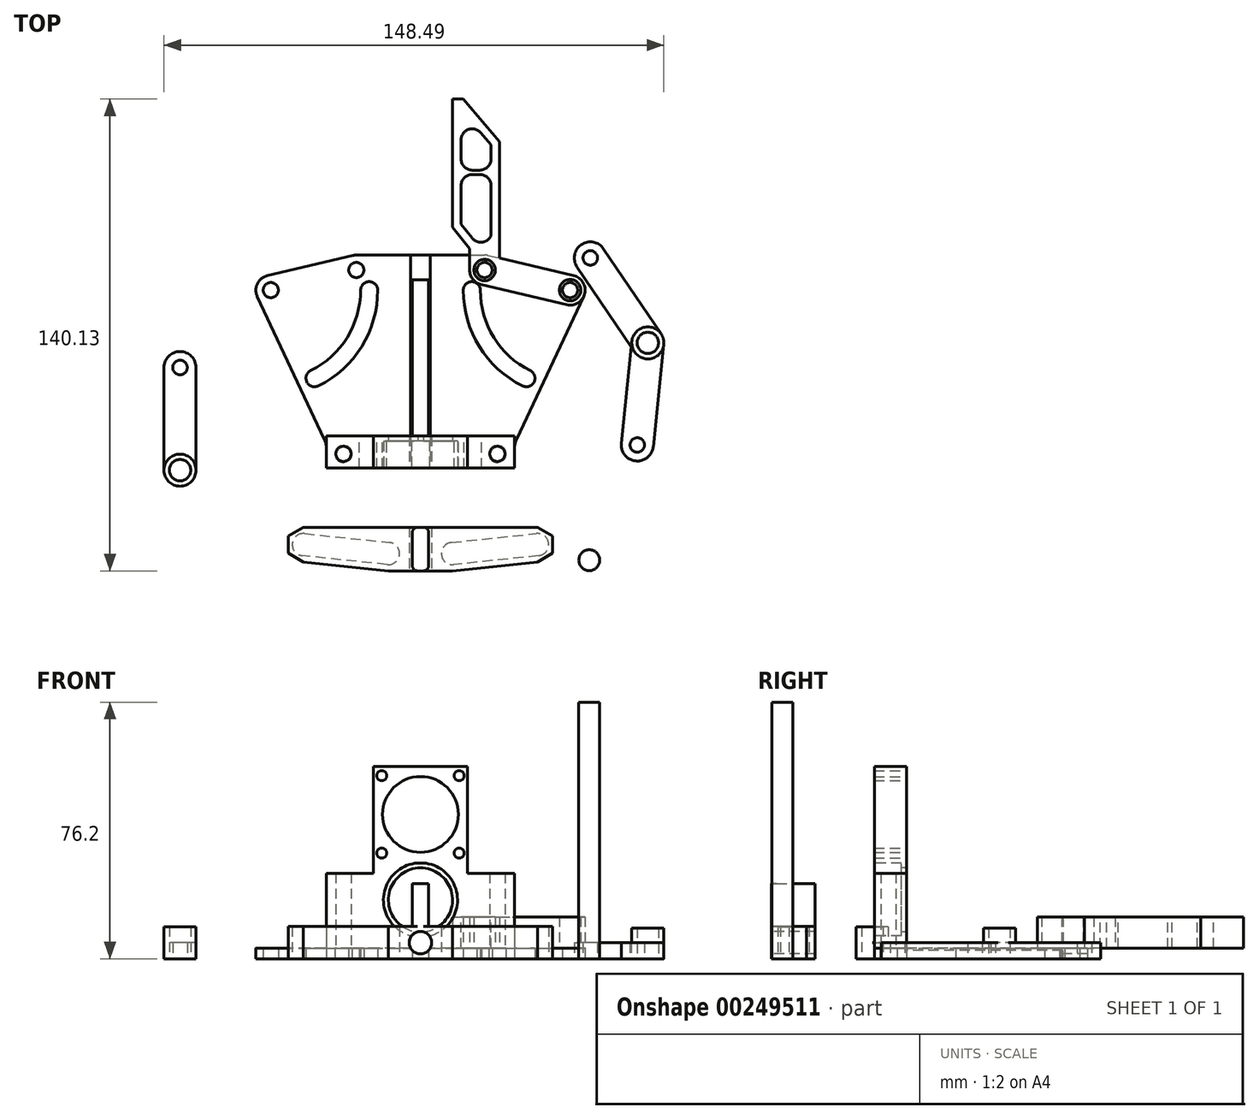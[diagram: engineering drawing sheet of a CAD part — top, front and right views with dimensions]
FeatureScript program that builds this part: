
annotation { "Feature Type Name" : "Feature", "Feature Type Description" : "" }
export const myFeature = defineFeature(function(context is Context, id is Id, definition is map)
    precondition{}
    {
        {
            var Q0;
            Q0=qCreatedBy(makeId("Top.planeOp"),FACE);
            var sketch = newSketch(context, id + "F0", { "sketchPlane" : qUnion([Q0])});
            skLineSegment(sketch, "E0", {"start": v(0, 0) * mm, "end": v(0, 58.8) * mm, "construction": true});
            skLineSegment(sketch, "E1", {"start": v(-19.05, 58.8) * mm, "end": v(19.05, 58.8) * mm, "construction": true});
            skLineSegment(sketch, "E2", {"start": v(-44.45, 52.83) * mm, "end": v(44.45, 52.83) * mm, "construction": true});
            skPoint(sketch, "E3", {"position": v(0, 52.83) * mm});
            skCircle(sketch, "E4", {"center": v(-19.05, 58.8) * mm, "radius": 2.25 * mm});
            skCircle(sketch, "E5", {"center": v(19.05, 58.8) * mm, "radius": 2.25 * mm});
            skCircle(sketch, "E6", {"center": v(44.45, 52.83) * mm, "radius": 2.25 * mm});
            skCircle(sketch, "E7", {"center": v(-44.45, 52.83) * mm, "radius": 2.25 * mm});
            skArc(sketch, "E8", {"start": v(-19.05, 63.25) * mm, "mid": v(-19.56, 63.22) * mm, "end": v(-20.07, 63.13) * mm});
            skArc(sketch, "E9", {"start": v(20.07, 63.13) * mm, "mid": v(19.56, 63.22) * mm, "end": v(19.05, 63.25) * mm});
            skArc(sketch, "E10", {"start": v(48.47, 50.94) * mm, "mid": v(48.45, 54.77) * mm, "end": v(45.47, 57.16) * mm});
            skArc(sketch, "E11", {"start": v(-45.47, 57.16) * mm, "mid": v(-48.45, 54.77) * mm, "end": v(-48.47, 50.94) * mm});
            skLineSegment(sketch, "E12", {"start": v(-28.57, 8.52) * mm, "end": v(-48.47, 50.94) * mm});
            skLineSegment(sketch, "E13", {"start": v(28.57, 8.52) * mm, "end": v(48.47, 50.94) * mm});
            skLineSegment(sketch, "E14", {"start": v(-45.47, 57.16) * mm, "end": v(-20.07, 63.13) * mm});
            skLineSegment(sketch, "E15", {"start": v(-19.05, 63.25) * mm, "end": v(19.05, 63.25) * mm});
            skLineSegment(sketch, "E16", {"start": v(20.07, 63.13) * mm, "end": v(45.47, 57.16) * mm});
            skPoint(sketch, "E17.visualSharp", {"position": v(-38.17, 49.74) * mm});
            skPoint(sketch, "E18.visualSharp", {"position": v(-18.53, 54.36) * mm});
            skPoint(sketch, "E19.visualSharp", {"position": v(38.17, 49.74) * mm});
            skCircle(sketch, "E20", {"center": v(-22.86, 4.2) * mm, "radius": 2.55 * mm});
            skCircle(sketch, "E21", {"center": v(22.86, 4.2) * mm, "radius": 2.55 * mm});
            skLineSegment(sketch, "E22.left", {"start": v(-27.94, 5.72) * mm, "end": v(-27.94, 0) * mm});
            skLineSegment(sketch, "E22.right", {"start": v(27.94, 5.72) * mm, "end": v(27.94, 0) * mm});
            skPoint(sketch, "E23.visualSharp", {"position": v(-27.94, 7.19) * mm});
            skArc(sketch, "E23.filletArc", {"start": v(-27.94, 5.72) * mm, "mid": v(-28.1, 7.15) * mm, "end": v(-28.57, 8.52) * mm});
            skPoint(sketch, "E24.visualSharp", {"position": v(27.94, 7.19) * mm});
            skArc(sketch, "E24.filletArc", {"start": v(28.57, 8.52) * mm, "mid": v(28.1, 7.15) * mm, "end": v(27.94, 5.72) * mm});
            skLineSegment(sketch, "E25", {"start": v(-27.94, 0) * mm, "end": v(-18.16, 0) * mm});
            skLineSegment(sketch, "E26.trimOffspring", {"start": v(18.16, 0) * mm, "end": v(27.94, 0) * mm});
            skLineSegment(sketch, "E27", {"start": v(-18.16, 0) * mm, "end": v(-18.16, 9.52) * mm});
            skLineSegment(sketch, "E28", {"start": v(18.16, 0) * mm, "end": v(18.16, 9.52) * mm});
            skLineSegment(sketch, "E29", {"start": v(-2.44, 55.89) * mm, "end": v(-2.44, 9.52) * mm});
            skLineSegment(sketch, "E30", {"start": v(-2.44, 9.52) * mm, "end": v(-18.16, 9.52) * mm});
            skLineSegment(sketch, "E31", {"start": v(18.16, 9.52) * mm, "end": v(2.44, 9.52) * mm});
            skLineSegment(sketch, "E32", {"start": v(2.44, 9.52) * mm, "end": v(2.44, 55.89) * mm});
            skLineSegment(sketch, "E33", {"start": v(-2.44, 55.89) * mm, "end": v(2.44, 55.89) * mm});
            skArc(sketch, "E34", {"start": v(15.24, 52.83) * mm, "mid": v(19.63, 37.44) * mm, "end": v(31.47, 26.67) * mm, "construction": true});
            skArc(sketch, "E35", {"start": v(17.78, 52.83) * mm, "mid": v(15.24, 55.37) * mm, "end": v(12.7, 52.83) * mm});
            skLineSegment(sketch, "E36", {"start": v(44.45, 52.83) * mm, "end": v(22.86, 4.2) * mm, "construction": true});
            skArc(sketch, "E37", {"start": v(32.6, 28.94) * mm, "mid": v(21.79, 38.78) * mm, "end": v(17.78, 52.83) * mm});
            skArc(sketch, "E38", {"start": v(12.7, 52.83) * mm, "mid": v(17.47, 36.1) * mm, "end": v(30.34, 24.39) * mm});
            skArc(sketch, "E39", {"start": v(30.34, 24.39) * mm, "mid": v(33.74, 25.54) * mm, "end": v(32.6, 28.94) * mm});
            skArc(sketch, "E40.MirrorCS", {"start": v(-30.34, 24.39) * mm, "mid": v(-33.74, 25.54) * mm, "end": v(-32.6, 28.94) * mm});
            skArc(sketch, "E41.MirrorCS", {"start": v(-32.6, 28.94) * mm, "mid": v(-21.79, 38.78) * mm, "end": v(-17.78, 52.83) * mm});
            skArc(sketch, "E42.MirrorCS", {"start": v(-12.7, 52.83) * mm, "mid": v(-17.47, 36.1) * mm, "end": v(-30.34, 24.39) * mm});
            skArc(sketch, "E43.MirrorCS", {"start": v(-17.78, 52.83) * mm, "mid": v(-15.24, 55.37) * mm, "end": v(-12.7, 52.83) * mm});
            skSolve(sketch);
        }
        {
            var Q0;
            Q0 = qSketchRegion(id + "F0", true);
            extrude(context, id + "F1", {"entities" : qUnion([Q0]), "depth" : 3.17 * mm});
        }
        {
            var Q0;
            Q0=qCreatedBy(makeId("Top.planeOp"),FACE);
            var sketch = newSketch(context, id + "F2", { "sketchPlane" : qUnion([Q0])});
            skCircle(sketch, "E44", {"center": v(-71.43, -0.63) * mm, "radius": 3.18 * mm});
            skCircle(sketch, "E45", {"center": v(-71.43, 29.85) * mm, "radius": 2.16 * mm});
            skCircle(sketch, "E46", {"center": v(-71.43, 29.85) * mm, "radius": 4.76 * mm});
            skCircle(sketch, "E47", {"center": v(-71.43, -0.63) * mm, "radius": 4.76 * mm});
            skLineSegment(sketch, "E48", {"start": v(-76.2, -0.63) * mm, "end": v(-76.2, 29.85) * mm});
            skLineSegment(sketch, "E49", {"start": v(-66.67, 29.85) * mm, "end": v(-66.67, -0.63) * mm});
            skSolve(sketch);
        }
        {
            var Q0;
            Q0 = qSketchRegion(id + "F2", true);
            extrude(context, id + "F3", {"entities" : qUnion([Q0]), "depth" : 4.76 * mm});
        }
        {
            var Q0;
            Q0=qCreatedBy(makeId("Top.planeOp"),FACE);
            var sketch = newSketch(context, id + "F4", { "sketchPlane" : qUnion([Q0])});
            skCircle(sketch, "E50", {"center": v(64.4, 6.85) * mm, "radius": 2.16 * mm});
            skCircle(sketch, "E51", {"center": v(67.54, 37.16) * mm, "radius": 3.18 * mm});
            skCircle(sketch, "E52", {"center": v(50.46, 62.4) * mm, "radius": 2.16 * mm});
            skLineSegment(sketch, "E53", {"start": v(50.46, 62.4) * mm, "end": v(67.54, 37.16) * mm, "construction": true});
            skLineSegment(sketch, "E54", {"start": v(67.54, 37.16) * mm, "end": v(64.4, 6.85) * mm, "construction": true});
            skArc(sketch, "E55", {"start": v(54.4, 65.08) * mm, "mid": v(47.79, 66.35) * mm, "end": v(46.51, 59.74) * mm});
            skArc(sketch, "E56", {"start": v(72.28, 36.67) * mm, "mid": v(72.16, 38.32) * mm, "end": v(71.48, 39.83) * mm});
            skLineSegment(sketch, "E57", {"start": v(54.4, 65.08) * mm, "end": v(71.48, 39.83) * mm});
            skLineSegment(sketch, "E58", {"start": v(72.28, 36.67) * mm, "end": v(69.14, 6.36) * mm});
            skLineSegment(sketch, "E59", {"start": v(59.66, 7.34) * mm, "end": v(62.62, 35.93) * mm});
            skLineSegment(sketch, "E60", {"start": v(62.62, 35.93) * mm, "end": v(46.51, 59.74) * mm});
            skCircle(sketch, "E61", {"center": v(64.4, 6.85) * mm, "radius": 4.76 * mm});
            skSolve(sketch);
        }
        {
            var Q0;
            Q0 = qSketchRegion(id + "F4", true);
            extrude(context, id + "F5", {"entities" : qUnion([Q0]), "depth" : 4.76 * mm});
        }
        {
            var Q0;
            Q0=makeQuery(id+"F1.opExtrude","CAP_FACE",FACE,{"disambiguationData":[OSD([sQuery(id+"F0.wireOp",EDGE,"E4"),sQuery(id+"F0.wireOp",EDGE,"E5"),sQuery(id+"F0.wireOp",EDGE,"E6"),sQuery(id+"F0.wireOp",EDGE,"E7"),sQuery(id+"F0.wireOp",EDGE,"E8"),sQuery(id+"F0.wireOp",EDGE,"E9"),sQuery(id+"F0.wireOp",EDGE,"E10"),sQuery(id+"F0.wireOp",EDGE,"E11"),sQuery(id+"F0.wireOp",EDGE,"CqgLeqqC-iIWA-dWGX-UMBu-9zdK8dDdMv7x"),sQuery(id+"F0.wireOp",EDGE,"E12"),sQuery(id+"F0.wireOp",EDGE,"E13"),sQuery(id+"F0.wireOp",EDGE,"E14"),sQuery(id+"F0.wireOp",EDGE,"E15"),sQuery(id+"F0.wireOp",EDGE,"E16"),sQuery(id+"F0.wireOp",EDGE,"d945b0c3-6755-44a5-947e-2b61b1ff6794.0"),sQuery(id+"F0.wireOp",EDGE,"d945b0c3-6755-44a5-947e-2b61b1ff6794.1"),sQuery(id+"F0.wireOp",EDGE,"d945b0c3-6755-44a5-947e-2b61b1ff6794.2"),sQuery(id+"F0.wireOp",EDGE,"d945b0c3-6755-44a5-947e-2b61b1ff6794.3"),sQuery(id+"F0.wireOp",EDGE,"d945b0c3-6755-44a5-947e-2b61b1ff6794.4"),sQuery(id+"F0.wireOp",EDGE,"d945b0c3-6755-44a5-947e-2b61b1ff6794.5"),sQuery(id+"F0.wireOp",EDGE,"E17.filletArc"),sQuery(id+"F0.wireOp",EDGE,"E18.filletArc"),sQuery(id+"F0.wireOp",EDGE,"d9db8587-809e-482b-9d1f-6ec99e13a1cb.filletArc"),sQuery(id+"F0.wireOp",EDGE,"E19.filletArc"),sQuery(id+"F0.wireOp",EDGE,"35a48806-880f-4cc7-b920-85be3e912b3a.filletArc"),sQuery(id+"F0.wireOp",EDGE,"24c7fc71-437c-45df-8c6e-ea73c7bb345a.filletArc")])],"isStart":false});
            var sketch = newSketch(context, id + "F6", { "sketchPlane" : qUnion([Q0])});
            skCircle(sketch, "E62", {"center": v(44.45, 52.83) * mm, "radius": 3.18 * mm});
            skCircle(sketch, "E63", {"center": v(19.05, 58.8) * mm, "radius": 3.18 * mm});
            skArc(sketch, "E64", {"start": v(43.43, 48.5) * mm, "mid": v(48.78, 51.82) * mm, "end": v(45.47, 57.16) * mm});
            skArc(sketch, "E65", {"start": v(14.6, 58.8) * mm, "mid": v(19.05, 54.36) * mm, "end": v(23.5, 58.8) * mm});
            skLineSegment(sketch, "E66", {"start": v(14.6, 58.8) * mm, "end": v(14.6, 65.15) * mm});
            skLineSegment(sketch, "E67", {"start": v(9.52, 109.6) * mm, "end": v(9.52, 71.5) * mm});
            skLineSegment(sketch, "E68", {"start": v(23.5, 96.9) * mm, "end": v(23.5, 58.8) * mm});
            skLineSegment(sketch, "E69", {"start": v(23.5, 62.32) * mm, "end": v(45.47, 57.16) * mm});
            skLineSegment(sketch, "E70", {"start": v(18.03, 54.47) * mm, "end": v(43.43, 48.5) * mm});
            skLineSegment(sketch, "E71", {"start": v(9.52, 71.5) * mm, "end": v(14.6, 65.15) * mm});
            skLineSegment(sketch, "E72", {"start": v(9.52, 109.6) * mm, "end": v(12.7, 109.6) * mm});
            skLineSegment(sketch, "E73", {"start": v(12.7, 109.6) * mm, "end": v(23.5, 96.9) * mm});
            skSolve(sketch);
        }
        {
            var Q0;
            Q0 = qSketchRegion(id + "F6", true);
            extrude(context, id + "F7", {"entities" : qUnion([Q0]), "depth" : 9.27 * mm});
        }
        {
            var Q0;
            Q0=makeQuery(id+"F1.opExtrude","CAP_FACE",FACE,{"disambiguationData":[OSD([sQuery(id+"F0.wireOp",EDGE,"E4"),sQuery(id+"F0.wireOp",EDGE,"E5"),sQuery(id+"F0.wireOp",EDGE,"E6"),sQuery(id+"F0.wireOp",EDGE,"E7"),sQuery(id+"F0.wireOp",EDGE,"E8"),sQuery(id+"F0.wireOp",EDGE,"E9"),sQuery(id+"F0.wireOp",EDGE,"E10"),sQuery(id+"F0.wireOp",EDGE,"E11"),sQuery(id+"F0.wireOp",EDGE,"CqgLeqqC-iIWA-dWGX-UMBu-9zdK8dDdMv7x"),sQuery(id+"F0.wireOp",EDGE,"E12"),sQuery(id+"F0.wireOp",EDGE,"E13"),sQuery(id+"F0.wireOp",EDGE,"E14"),sQuery(id+"F0.wireOp",EDGE,"E15"),sQuery(id+"F0.wireOp",EDGE,"E16"),sQuery(id+"F0.wireOp",EDGE,"d945b0c3-6755-44a5-947e-2b61b1ff6794.0"),sQuery(id+"F0.wireOp",EDGE,"d945b0c3-6755-44a5-947e-2b61b1ff6794.1"),sQuery(id+"F0.wireOp",EDGE,"d945b0c3-6755-44a5-947e-2b61b1ff6794.2"),sQuery(id+"F0.wireOp",EDGE,"d945b0c3-6755-44a5-947e-2b61b1ff6794.3"),sQuery(id+"F0.wireOp",EDGE,"d945b0c3-6755-44a5-947e-2b61b1ff6794.4"),sQuery(id+"F0.wireOp",EDGE,"d945b0c3-6755-44a5-947e-2b61b1ff6794.5"),sQuery(id+"F0.wireOp",EDGE,"E17.filletArc"),sQuery(id+"F0.wireOp",EDGE,"E18.filletArc"),sQuery(id+"F0.wireOp",EDGE,"d9db8587-809e-482b-9d1f-6ec99e13a1cb.filletArc"),sQuery(id+"F0.wireOp",EDGE,"E19.filletArc"),sQuery(id+"F0.wireOp",EDGE,"35a48806-880f-4cc7-b920-85be3e912b3a.filletArc"),sQuery(id+"F0.wireOp",EDGE,"24c7fc71-437c-45df-8c6e-ea73c7bb345a.filletArc"),sQuery(id+"F0.wireOp",EDGE,"E20"),sQuery(id+"F0.wireOp",EDGE,"E21")])],"isStart":false});
            var sketch = newSketch(context, id + "F8", { "sketchPlane" : qUnion([Q0])});
            skCircle(sketch, "E74.0", {"center": v(-22.86, 4.2) * mm, "radius": 2.55 * mm, "construction": true});
            skCircle(sketch, "E75.0", {"center": v(22.86, 4.2) * mm, "radius": 2.55 * mm, "construction": true});
            skCircle(sketch, "E76", {"center": v(-22.86, 4.2) * mm, "radius": 2.25 * mm});
            skCircle(sketch, "E77", {"center": v(22.86, 4.2) * mm, "radius": 2.25 * mm});
            skLineSegment(sketch, "E78.bottom", {"start": v(-27.94, 0) * mm, "end": v(27.94, 0) * mm});
            skLineSegment(sketch, "E78.top", {"start": v(-27.94, 9.52) * mm, "end": v(27.94, 9.53) * mm});
            skLineSegment(sketch, "E78.left", {"start": v(-27.94, 0) * mm, "end": v(-27.94, 9.52) * mm});
            skLineSegment(sketch, "E78.right", {"start": v(27.94, 0) * mm, "end": v(27.94, 9.53) * mm});
            skSolve(sketch);
        }
        {
            var Q0;
            Q0 = qSketchRegion(id + "F8", true);
            extrude(context, id + "F9", {"entities" : qUnion([Q0]), "depth" : 22.22 * mm});
        }
        {
            var Q0;
            Q0=makeQuery(id+"F9.opExtrude","CAP_FACE",FACE,{"disambiguationData":[OSD([sQuery(id+"F8.wireOp",EDGE,"E76"),sQuery(id+"F8.wireOp",EDGE,"E77"),sQuery(id+"F8.wireOp",EDGE,"E78.bottom"),sQuery(id+"F8.wireOp",EDGE,"E78.top"),sQuery(id+"F8.wireOp",EDGE,"E78.left"),sQuery(id+"F8.wireOp",EDGE,"E78.right")])],"isStart":false});
            var sketch = newSketch(context, id + "F10", { "sketchPlane" : qUnion([Q0])});
            skLineSegment(sketch, "E79.bottom", {"start": v(-14, 9.52) * mm, "end": v(14, 9.53) * mm});
            skLineSegment(sketch, "E79.top", {"start": v(-14, 0) * mm, "end": v(14, 0) * mm});
            skLineSegment(sketch, "E79.left", {"start": v(-14, 9.52) * mm, "end": v(-14, 0) * mm});
            skLineSegment(sketch, "E79.right", {"start": v(14, 9.52) * mm, "end": v(14, 0) * mm});
            skLineSegment(sketch, "E80", {"start": v(0, 9.53) * mm, "end": v(0, 0) * mm, "construction": true});
            skSolve(sketch);
        }
        {
            var Q0;
            Q0 = qSketchRegion(id + "F10", true);
            extrude(context, id + "F11", {"entities" : qUnion([Q0]), "operationType" : NewBodyOperationType.ADD, "depth" : 31.75 * mm});
        }
        {
            var Q0;
            Q0=makeQuery(id+"F9.opExtrude","SWEPT_FACE",FACE,{"disambiguationData":[OSD([sQuery(id+"F8.wireOp",EDGE,"E78.bottom")])]});
            var sketch = newSketch(context, id + "F12", { "sketchPlane" : qUnion([Q0])});
            skCircle(sketch, "E81", {"center": v(0, 17.46) * mm, "radius": 11 * mm});
            skSolve(sketch);
        }
        {
            var Q0;
            Q0 = qSketchRegion(id + "F12", true);
            extrude(context, id + "F13", {"entities" : qUnion([Q0]), "operationType" : NewBodyOperationType.REMOVE, "oppositeDirection" : true, "depth" : 8 * mm});
        }
        {
            var Q0;
            Q0=makeQuery(id+"F13.boolean.opBoolean","COPY",FACE,{"derivedFrom":makeQuery(id+"F13.opExtrude","CAP_FACE",FACE,{"disambiguationData":[OSD([sQuery(id+"F12.wireOp",EDGE,"E81")])],"isStart":false})});
            var sketch = newSketch(context, id + "F14", { "sketchPlane" : qUnion([Q0])});
            skCircle(sketch, "E82", {"center": v(0, 17.46) * mm, "radius": 9.52 * mm});
            skSolve(sketch);
        }
        {
            var Q0;
            Q0 = qSketchRegion(id + "F14", true);
            extrude(context, id + "F15", {"entities" : qUnion([Q0]), "operationType" : NewBodyOperationType.REMOVE, "endBound" : BoundingType.THROUGH_ALL, "oppositeDirection" : true, "depth" : 25.4 * mm});
        }
        {
            var Q0;
            Q0=makeQuery(id+"F11.boolean.opBoolean","MERGE",FACE,{"derivedFrom":[makeQuery(id+"FUQhWkX4n9esXz3_5.opExtrude","SWEPT_FACE",FACE,{"disambiguationData":[OSD([sQuery(id+"Fk6gKunzgzx0A8n_5.wireOp",EDGE,"760f4b6c-e456-44f3-9e5d-a07d3b660167.0")])]}),makeQuery(id+"F11.opExtrude","SWEPT_FACE",FACE,{"disambiguationData":[OSD([sQuery(id+"F10.wireOp",EDGE,"E79.bottom")])]})]});
            var sketch = newSketch(context, id + "F16", { "sketchPlane" : qUnion([Q0])});
            skCircle(sketch, "E83.0", {"center": v(0, 17.46) * mm, "radius": 9.52 * mm, "construction": true});
            skCircle(sketch, "E84", {"center": v(0, 42.86) * mm, "radius": 11.25 * mm});
            skLineSegment(sketch, "E85.bottom", {"start": v(-11.5, 54.36) * mm, "end": v(11.5, 54.36) * mm, "construction": true});
            skLineSegment(sketch, "E85.top", {"start": v(-11.5, 31.36) * mm, "end": v(11.5, 31.36) * mm, "construction": true});
            skLineSegment(sketch, "E85.left", {"start": v(-11.5, 54.36) * mm, "end": v(-11.5, 31.36) * mm, "construction": true});
            skLineSegment(sketch, "E85.right", {"start": v(11.5, 54.36) * mm, "end": v(11.5, 31.36) * mm, "construction": true});
            skLineSegment(sketch, "E86", {"start": v(-11.5, 54.36) * mm, "end": v(11.5, 31.36) * mm, "construction": true});
            skLineSegment(sketch, "E87.bottom", {"start": v(14.5, 57.36) * mm, "end": v(-14.5, 57.36) * mm, "construction": true});
            skLineSegment(sketch, "E87.top", {"start": v(14.5, 28.36) * mm, "end": v(-14.5, 28.36) * mm, "construction": true});
            skLineSegment(sketch, "E87.left", {"start": v(14.5, 57.36) * mm, "end": v(14.5, 28.36) * mm, "construction": true});
            skLineSegment(sketch, "E87.right", {"start": v(-14.5, 57.36) * mm, "end": v(-14.5, 28.36) * mm, "construction": true});
            skLineSegment(sketch, "E88", {"start": v(-14.5, 28.36) * mm, "end": v(14.5, 57.36) * mm, "construction": true});
            skCircle(sketch, "E89", {"center": v(11.5, 54.36) * mm, "radius": 1.5 * mm});
            skCircle(sketch, "E90", {"center": v(11.5, 31.36) * mm, "radius": 1.5 * mm});
            skCircle(sketch, "E91", {"center": v(-11.5, 31.36) * mm, "radius": 1.5 * mm});
            skCircle(sketch, "E92", {"center": v(-11.5, 54.36) * mm, "radius": 1.5 * mm});
            skSolve(sketch);
        }
        {
            var Q0;
            Q0 = qSketchRegion(id + "F16", true);
            extrude(context, id + "F17", {"entities" : qUnion([Q0]), "operationType" : NewBodyOperationType.REMOVE, "endBound" : BoundingType.THROUGH_ALL, "oppositeDirection" : true, "depth" : 25.4 * mm});
        }
        {
            var Q0;
            Q0=qCreatedBy(makeId("Top.planeOp"),FACE);
            var sketch = newSketch(context, id + "F18", { "sketchPlane" : qUnion([Q0])});
            skLineSegment(sketch, "E93", {"start": v(-9.52, -25.4) * mm, "end": v(9.52, -25.4) * mm, "construction": true});
            skLineSegment(sketch, "E94", {"start": v(9.52, -25.4) * mm, "end": v(34.79, -22.74) * mm, "construction": true});
            skLineSegment(sketch, "E95", {"start": v(-9.52, -25.4) * mm, "end": v(-34.79, -22.74) * mm, "construction": true});
            skArc(sketch, "E96", {"start": v(-9.87, -28.68) * mm, "mid": v(-6.24, -25.75) * mm, "end": v(-9.18, -22.12) * mm});
            skArc(sketch, "E97", {"start": v(9.18, -22.12) * mm, "mid": v(6.24, -25.75) * mm, "end": v(9.87, -28.68) * mm});
            skArc(sketch, "E98", {"start": v(35.13, -26.03) * mm, "mid": v(38.07, -22.4) * mm, "end": v(34.44, -19.46) * mm});
            skArc(sketch, "E99", {"start": v(-34.44, -19.46) * mm, "mid": v(-38.07, -22.4) * mm, "end": v(-35.13, -26.03) * mm});
            skLineSegment(sketch, "E100", {"start": v(-34.44, -19.46) * mm, "end": v(-9.18, -22.12) * mm});
            skLineSegment(sketch, "E101", {"start": v(9.18, -22.12) * mm, "end": v(34.44, -19.46) * mm});
            skLineSegment(sketch, "E102", {"start": v(35.13, -26.03) * mm, "end": v(9.87, -28.68) * mm});
            skLineSegment(sketch, "E103", {"start": v(-9.87, -28.68) * mm, "end": v(-35.13, -26.03) * mm});
            skPoint(sketch, "E104", {"position": v(0, -25.4) * mm});
            skArc(sketch, "E105.cCircle", {"start": v(-32.17, -26.34) * mm, "mid": v(-37.2, -19.02) * mm, "end": v(-32.56, -26.6) * mm, "construction": true});
            skLineSegment(sketch, "E105.2", {"start": v(-34.79, -27.88) * mm, "end": v(-39.23, -25.31) * mm});
            skLineSegment(sketch, "E105.3", {"start": v(-39.23, -25.31) * mm, "end": v(-39.23, -20.18) * mm});
            skLineSegment(sketch, "E105.4", {"start": v(-39.23, -20.18) * mm, "end": v(-34.79, -17.61) * mm});
            skPoint(sketch, "E105.0.midPoint", {"position": v(-30.34, -22.74) * mm});
            skCircle(sketch, "E106.cCircle", {"center": v(34.79, -22.74) * mm, "radius": 4.45 * mm, "construction": true});
            skLineSegment(sketch, "E106.0", {"start": v(34.79, -17.61) * mm, "end": v(39.23, -20.18) * mm});
            skLineSegment(sketch, "E106.1", {"start": v(39.23, -20.18) * mm, "end": v(39.23, -25.31) * mm});
            skLineSegment(sketch, "E106.2", {"start": v(39.23, -25.31) * mm, "end": v(34.79, -27.88) * mm});
            skPoint(sketch, "E106.0.midPoint", {"position": v(37, -18.9) * mm});
            skLineSegment(sketch, "E107", {"start": v(34.79, -27.88) * mm, "end": v(9.52, -30.53) * mm});
            skLineSegment(sketch, "E108", {"start": v(9.52, -30.53) * mm, "end": v(-9.53, -30.53) * mm});
            skLineSegment(sketch, "E109", {"start": v(-9.52, -30.53) * mm, "end": v(-34.79, -27.88) * mm});
            skPoint(sketch, "E110.orphan", {"position": v(-30.34, -20.18) * mm});
            skPoint(sketch, "E111.orphan", {"position": v(-30.34, -25.31) * mm});
            skLineSegment(sketch, "E112", {"start": v(-34.79, -17.61) * mm, "end": v(34.79, -17.61) * mm});
            skSolve(sketch);
        }
        {
            var Q0;
            Q0 = qSketchRegion(id + "F18", true);
            extrude(context, id + "F19", {"entities" : qUnion([Q0]), "depth" : 9.52 * mm});
        }
        {
            var Q0;
            Q0=makeQuery(id+"F19.opExtrude","SWEPT_FACE",FACE,{"disambiguationData":[OSD([sQuery(id+"F18.wireOp",EDGE,"E108")])]});
            var sketch = newSketch(context, id + "F20", { "sketchPlane" : qUnion([Q0])});
            skCircle(sketch, "E113", {"center": v(0, 4.76) * mm, "radius": 3.32 * mm});
            skSolve(sketch);
        }
        {
            var Q0;
            Q0 = qSketchRegion(id + "F20", true);
            extrude(context, id + "F21", {"entities" : qUnion([Q0]), "operationType" : NewBodyOperationType.REMOVE, "endBound" : BoundingType.THROUGH_ALL, "oppositeDirection" : true, "depth" : 25.4 * mm});
        }
        {
            var Q0;
            Q0=qCreatedBy(makeId("Top.planeOp"),FACE);
            var sketch = newSketch(context, id + "F22", { "sketchPlane" : qUnion([Q0])});
            skCircle(sketch, "E114", {"center": v(50.14, -27.37) * mm, "radius": 3.1 * mm});
            skSolve(sketch);
        }
        {
            var Q0;
            Q0 = qSketchRegion(id + "F22", true);
            extrude(context, id + "F23", {"entities" : qUnion([Q0]), "depth" : 76.2 * mm});
        }
        {
            var Q0;
            Q0=makeQuery(id+"F19.opExtrude","CAP_FACE",FACE,{"disambiguationData":[OSD([sQuery(id+"F18.wireOp",EDGE,"E96"),sQuery(id+"F18.wireOp",EDGE,"E97"),sQuery(id+"F18.wireOp",EDGE,"E98"),sQuery(id+"F18.wireOp",EDGE,"E99"),sQuery(id+"F18.wireOp",EDGE,"E100"),sQuery(id+"F18.wireOp",EDGE,"E101"),sQuery(id+"F18.wireOp",EDGE,"E102"),sQuery(id+"F18.wireOp",EDGE,"E103"),sQuery(id+"F18.wireOp",EDGE,"E105.2"),sQuery(id+"F18.wireOp",EDGE,"E105.3"),sQuery(id+"F18.wireOp",EDGE,"E105.4"),sQuery(id+"F18.wireOp",EDGE,"E106.0"),sQuery(id+"F18.wireOp",EDGE,"E106.1"),sQuery(id+"F18.wireOp",EDGE,"E106.2"),sQuery(id+"F18.wireOp",EDGE,"E107"),sQuery(id+"F18.wireOp",EDGE,"E108"),sQuery(id+"F18.wireOp",EDGE,"E109"),sQuery(id+"F18.wireOp",EDGE,"E112")])],"isStart":false});
            var sketch = newSketch(context, id + "F24", { "sketchPlane" : qUnion([Q0])});
            skLineSegment(sketch, "E115.0.0", {"start": v(-9.52, -30.53) * mm, "end": v(9.52, -30.53) * mm});
            skLineSegment(sketch, "E115.0.1", {"start": v(9.52, -30.53) * mm, "end": v(34.79, -27.88) * mm});
            skLineSegment(sketch, "E115.0.2", {"start": v(34.79, -27.88) * mm, "end": v(39.23, -25.31) * mm});
            skLineSegment(sketch, "E115.0.3", {"start": v(39.23, -25.31) * mm, "end": v(39.23, -20.18) * mm});
            skLineSegment(sketch, "E115.0.4", {"start": v(39.23, -20.18) * mm, "end": v(34.79, -17.61) * mm});
            skLineSegment(sketch, "E115.0.5", {"start": v(34.79, -17.61) * mm, "end": v(-34.79, -17.61) * mm});
            skLineSegment(sketch, "E115.0.6", {"start": v(-34.79, -17.61) * mm, "end": v(-39.23, -20.18) * mm});
            skLineSegment(sketch, "E115.0.7", {"start": v(-39.23, -20.18) * mm, "end": v(-39.23, -25.31) * mm});
            skLineSegment(sketch, "E115.0.8", {"start": v(-39.23, -25.31) * mm, "end": v(-34.79, -27.88) * mm});
            skLineSegment(sketch, "E115.0.9", {"start": v(-34.79, -27.88) * mm, "end": v(-9.52, -30.53) * mm});
            skSolve(sketch);
        }
        {
            var Q0;
            Q0 = qSketchRegion(id + "F24", true);
            extrude(context, id + "F25", {"entities" : qUnion([Q0]), "operationType" : NewBodyOperationType.ADD, "depth" : 0.03 * mm});
        }
        {
            var Q0;
            Q0=makeQuery(id+"F25.opExtrude","CAP_FACE",FACE,{"disambiguationData":[OSD([sQuery(id+"F24.wireOp",EDGE,"E115.0.0"),sQuery(id+"F24.wireOp",EDGE,"E115.0.1"),sQuery(id+"F24.wireOp",EDGE,"E115.0.2"),sQuery(id+"F24.wireOp",EDGE,"E115.0.3"),sQuery(id+"F24.wireOp",EDGE,"E115.0.4"),sQuery(id+"F24.wireOp",EDGE,"E115.0.5"),sQuery(id+"F24.wireOp",EDGE,"E115.0.6"),sQuery(id+"F24.wireOp",EDGE,"E115.0.7"),sQuery(id+"F24.wireOp",EDGE,"E115.0.8"),sQuery(id+"F24.wireOp",EDGE,"E115.0.9")])],"isStart":false});
            var sketch = newSketch(context, id + "F26", { "sketchPlane" : qUnion([Q0])});
            skLineSegment(sketch, "E116.bottom", {"start": v(0.89, -30.53) * mm, "end": v(-0.89, -30.53) * mm});
            skLineSegment(sketch, "E116.top", {"start": v(0.89, -17.61) * mm, "end": v(-0.89, -17.61) * mm});
            skLineSegment(sketch, "E116.left", {"start": v(2.41, -29) * mm, "end": v(2.41, -19.14) * mm});
            skLineSegment(sketch, "E116.right", {"start": v(-2.41, -29) * mm, "end": v(-2.41, -19.14) * mm});
            skPoint(sketch, "E117.visualSharp", {"position": v(2.41, -30.53) * mm});
            skArc(sketch, "E117.filletArc", {"start": v(0.89, -30.53) * mm, "mid": v(1.97, -30.09) * mm, "end": v(2.41, -29) * mm});
            skPoint(sketch, "E118.visualSharp", {"position": v(-2.41, -30.53) * mm});
            skArc(sketch, "E118.filletArc", {"start": v(-2.41, -29) * mm, "mid": v(-1.97, -30.09) * mm, "end": v(-0.89, -30.53) * mm});
            skPoint(sketch, "E119.visualSharp", {"position": v(-2.41, -17.61) * mm});
            skArc(sketch, "E119.filletArc", {"start": v(-0.89, -17.61) * mm, "mid": v(-1.97, -18.06) * mm, "end": v(-2.41, -19.14) * mm});
            skPoint(sketch, "E120.visualSharp", {"position": v(2.41, -17.61) * mm});
            skArc(sketch, "E120.filletArc", {"start": v(2.41, -19.14) * mm, "mid": v(1.97, -18.06) * mm, "end": v(0.89, -17.61) * mm});
            skSolve(sketch);
        }
        {
            var Q0;
            Q0 = qSketchRegion(id + "F26", true);
            extrude(context, id + "F27", {"entities" : qUnion([Q0]), "operationType" : NewBodyOperationType.ADD, "depth" : 12.7 * mm});
        }
        {
            var Q0;
            Q0=makeQuery(id+"F3.opExtrude","CAP_FACE",FACE,{"disambiguationData":[OSD([sQuery(id+"F2.wireOp",EDGE,"E44"),sQuery(id+"F2.wireOp",EDGE,"E45"),sQuery(id+"F2.wireOp",EDGE,"E46"),sQuery(id+"F2.wireOp",EDGE,"E47"),sQuery(id+"F2.wireOp",EDGE,"E48"),sQuery(id+"F2.wireOp",EDGE,"E49")])],"isStart":false});
            var sketch = newSketch(context, id + "F28", { "sketchPlane" : qUnion([Q0])});
            skCircle(sketch, "E121", {"center": v(-71.43, -0.63) * mm, "radius": 4.76 * mm});
            skCircle(sketch, "E122", {"center": v(-71.43, -0.63) * mm, "radius": 3.18 * mm});
            skSolve(sketch);
        }
        {
            var Q0;
            Q0 = qSketchRegion(id + "F28", true);
            extrude(context, id + "F29", {"entities" : qUnion([Q0]), "operationType" : NewBodyOperationType.ADD, "depth" : 4.76 * mm});
        }
        {
            var Q0;
            Q0=makeQuery(id+"F5.opExtrude","CAP_FACE",FACE,{"disambiguationData":[OSD([sQuery(id+"F4.wireOp",EDGE,"E50"),sQuery(id+"F4.wireOp",EDGE,"E51"),sQuery(id+"F4.wireOp",EDGE,"E52"),sQuery(id+"F4.wireOp",EDGE,"E55"),sQuery(id+"F4.wireOp",EDGE,"E56"),sQuery(id+"F4.wireOp",EDGE,"bscZtk6X-J7Kt-JnbV-Olq2-uJptXNIgswE4"),sQuery(id+"F4.wireOp",EDGE,"E57"),sQuery(id+"F4.wireOp",EDGE,"E58"),sQuery(id+"F4.wireOp",EDGE,"E59"),sQuery(id+"F4.wireOp",EDGE,"E60")])],"isStart":false});
            var sketch = newSketch(context, id + "F30", { "sketchPlane" : qUnion([Q0])});
            skCircle(sketch, "E123", {"center": v(67.54, 37.16) * mm, "radius": 4.76 * mm});
            skCircle(sketch, "E124", {"center": v(67.54, 37.16) * mm, "radius": 3.18 * mm});
            skSolve(sketch);
        }
        {
            var Q0;
            Q0 = qSketchRegion(id + "F30", true);
            extrude(context, id + "F31", {"entities" : qUnion([Q0]), "operationType" : NewBodyOperationType.ADD, "depth" : 4.38 * mm});
        }
        {
            var Q0;
            Q0=makeQuery(id+"F7.opExtrude","CAP_FACE",FACE,{"disambiguationData":[OSD([sQuery(id+"F6.wireOp",EDGE,"E62"),sQuery(id+"F6.wireOp",EDGE,"E63"),sQuery(id+"F6.wireOp",EDGE,"E64"),sQuery(id+"F6.wireOp",EDGE,"E65"),sQuery(id+"F6.wireOp",EDGE,"E66"),sQuery(id+"F6.wireOp",EDGE,"E67"),sQuery(id+"F6.wireOp",EDGE,"E68"),sQuery(id+"F6.wireOp",EDGE,"E69"),sQuery(id+"F6.wireOp",EDGE,"E70"),sQuery(id+"F6.wireOp",EDGE,"E71"),sQuery(id+"F6.wireOp",EDGE,"E72"),sQuery(id+"F6.wireOp",EDGE,"E73")])],"isStart":false});
            var sketch = newSketch(context, id + "F32", { "sketchPlane" : qUnion([Q0])});
            skLineSegment(sketch, "E125.0", {"start": v(12.06, 72.4) * mm, "end": v(15.35, 68.28) * mm});
            skLineSegment(sketch, "E125.1", {"start": v(20.95, 95.97) * mm, "end": v(20.95, 91.77) * mm});
            skLineSegment(sketch, "E125.2", {"start": v(17.88, 99.58) * mm, "end": v(20.95, 95.97) * mm});
            skLineSegment(sketch, "E125.4", {"start": v(12.06, 97.44) * mm, "end": v(12.06, 91.77) * mm});
            skPoint(sketch, "E126.visualSharp", {"position": v(12.06, 106.43) * mm});
            skArc(sketch, "E126.filletArc", {"start": v(17.88, 99.58) * mm, "mid": v(14.23, 100.54) * mm, "end": v(12.06, 97.44) * mm});
            skArc(sketch, "E127", {"start": v(15.35, 68.28) * mm, "mid": v(18.36, 67.07) * mm, "end": v(20.95, 69.02) * mm});
            skLineSegment(sketch, "E128", {"start": v(15.37, 88.47) * mm, "end": v(17.65, 88.47) * mm});
            skLineSegment(sketch, "E129", {"start": v(15.37, 87.2) * mm, "end": v(17.65, 87.2) * mm});
            skLineSegment(sketch, "E130.trimOffspring", {"start": v(20.95, 83.9) * mm, "end": v(20.95, 69.02) * mm});
            skLineSegment(sketch, "E131.trimOffspring", {"start": v(12.06, 83.9) * mm, "end": v(12.06, 72.4) * mm});
            skPoint(sketch, "E132.visualSharp", {"position": v(12.06, 87.2) * mm});
            skArc(sketch, "E132.filletArc", {"start": v(15.37, 87.2) * mm, "mid": v(13.03, 86.23) * mm, "end": v(12.06, 83.9) * mm});
            skPoint(sketch, "E133.visualSharp", {"position": v(20.95, 87.2) * mm});
            skArc(sketch, "E133.filletArc", {"start": v(20.95, 83.9) * mm, "mid": v(19.99, 86.23) * mm, "end": v(17.65, 87.2) * mm});
            skPoint(sketch, "E134.visualSharp", {"position": v(12.06, 88.47) * mm});
            skArc(sketch, "E134.filletArc", {"start": v(12.06, 91.77) * mm, "mid": v(13.03, 89.43) * mm, "end": v(15.37, 88.47) * mm});
            skPoint(sketch, "E135.visualSharp", {"position": v(20.95, 88.47) * mm});
            skArc(sketch, "E135.filletArc", {"start": v(17.65, 88.47) * mm, "mid": v(19.99, 89.43) * mm, "end": v(20.95, 91.77) * mm});
            skLineSegment(sketch, "E136", {"start": v(19.05, 58.8) * mm, "end": v(44.45, 52.83) * mm, "construction": true});
            skSolve(sketch);
        }
        {
            var Q0;
            Q0 = qSketchRegion(id + "F32", true);
            extrude(context, id + "F33", {"entities" : qUnion([Q0]), "operationType" : NewBodyOperationType.REMOVE, "endBound" : BoundingType.THROUGH_ALL, "oppositeDirection" : true, "depth" : 25.4 * mm});
        }
    });
